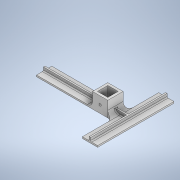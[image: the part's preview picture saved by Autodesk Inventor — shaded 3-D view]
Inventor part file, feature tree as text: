
AUTODESK INVENTOR PART (.ipt)
format: ipt  version: 2020 (Build 240168000, 168)  size: 227,840 bytes
history: native  units: mm
features: sketch x5, extrude x4, projected_geometry x3, fillet x2, hole x1
ambient origin geometry x8: Origin, YZ Plane, XZ Plane, XY Plane, X Axis, Y Axis, Z Axis, Center Point
bodies: Solid1 (feature_tree)
feature tree (15):
  extrude  "Extrusion1"  Depth=30.0mm
  extrude  "Extrusion2"  Depth=30.0mm
  extrude  "Extrusion3"  Depth=30.0mm
  fillet  "Fillet1"  Radius=30.0mm
  hole  "Hole1"  [1 undecoded]
  extrude  "Extrusion4"  Depth=2.0mm
  fillet  "Fillet2"  [1 undecoded]
  sketch  "Sketch1"  dims[d0=150.0mm d1=30.0mm]
  sketch  "Sketch2"  dims[d2=150.0mm d3=30.0mm]
  sketch  "Sketch4"  dims[d4=3.0mm d5=0.0mm d6=30.0mm d7=30.0mm]
  projected_geometry  "Projected Loop1"
  sketch  "Sketch5"  dims[d8=40.0mm d9=30.0mm d10=0.0mm]
  projected_geometry  "Projected Loop2"
  sketch  "Sketch6"  dims[d11=20.25mm d12=20.25mm d13=0.0mm d14=0.0mm d15=10.0mm d16=15.0mm d17=4.3mm d18=6.0mm d19=9.4mm d20=2.0mm d21=90.0deg d22=8.0mm d23=90.0deg d24=3.0mm d25=3.0mm d26=3.0mm d27=10.0mm d28=0.0mm d29=2.0mm]
  projected_geometry  "Projected Loop3"
note: 2 required parameter values undecoded (feature->parameter linkage not recoverable at this tier; creation-order binding heuristic only, values carry confidence <= 0.55)
